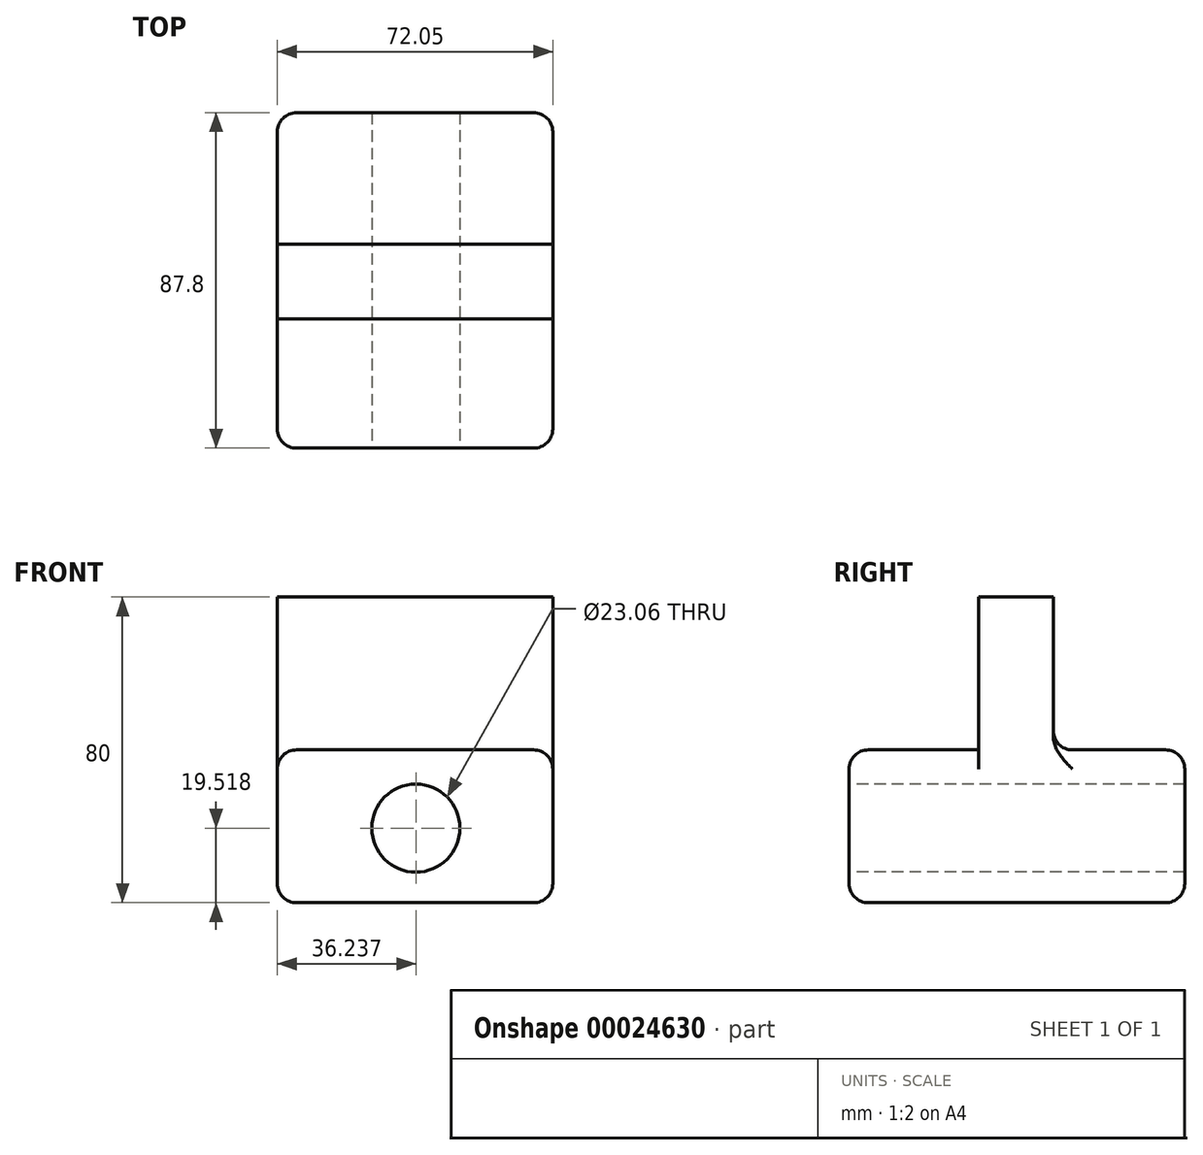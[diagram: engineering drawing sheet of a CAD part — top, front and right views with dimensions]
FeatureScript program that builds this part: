
annotation { "Feature Type Name" : "Feature", "Feature Type Description" : "" }
export const myFeature = defineFeature(function(context is Context, id is Id, definition is map)
    precondition{}
    {
        {
            var Q0;
            Q0=qCreatedBy(makeId("Top.planeOp"),FACE);
            var sketch = newSketch(context, id + "F0", { "sketchPlane" : qUnion([Q0])});
            skLineSegment(sketch, "E0.bottom", {"start": v(-59.89, -44.54) * mm, "end": v(12.16, -44.54) * mm});
            skLineSegment(sketch, "E0.top", {"start": v(-59.89, 43.26) * mm, "end": v(12.16, 43.26) * mm});
            skLineSegment(sketch, "E0.left", {"start": v(-59.89, -44.54) * mm, "end": v(-59.89, 43.26) * mm});
            skLineSegment(sketch, "E0.right", {"start": v(12.16, -44.54) * mm, "end": v(12.16, 43.26) * mm});
            skSolve(sketch);
        }
        {
            var Q0;
            Q0=makeQuery(id+"F0.imprint","IMPRINT",FACE,{"disambiguationData":[TD([[makeQuery(id+"F0.imprint","IMPRINT",EDGE,{"derivedFrom":sQuery(id+"F0.wireOp",EDGE,"E0.bottom")}),1.0]])]});
            extrude(context, id + "F1", {"entities" : qUnion([Q0]), "depth" : 40 * mm});
        }
        {
            var Q0;
            Q0=makeQuery(id+"F1.opExtrude","SWEPT_FACE",FACE,{"disambiguationData":[OSD([sQuery(id+"F0.wireOp",EDGE,"E0.bottom")])]});
            var sketch = newSketch(context, id + "F2", { "sketchPlane" : qUnion([Q0])});
            skCircle(sketch, "E1", {"center": v(-23.65, 19.52) * mm, "radius": 11.53 * mm});
            skSolve(sketch);
        }
        {
            var Q0;
            Q0=makeQuery(id+"F2.imprint","IMPRINT",FACE,{"disambiguationData":[TD([[makeQuery(id+"F2.imprint","IMPRINT",EDGE,{"derivedFrom":sQuery(id+"F2.wireOp",EDGE,"E1")}),1.0]])]});
            extrude(context, id + "F3", {"entities" : qUnion([Q0]), "operationType" : NewBodyOperationType.REMOVE, "endBound" : BoundingType.THROUGH_ALL, "oppositeDirection" : true, "depth" : 25 * mm});
        }
        {
            var Q0;
            Q0=makeQuery(id+"F1.opExtrude","CAP_FACE",FACE,{"disambiguationData":[OSD([sQuery(id+"F0.wireOp",EDGE,"E0.bottom"),sQuery(id+"F0.wireOp",EDGE,"E0.top"),sQuery(id+"F0.wireOp",EDGE,"E0.left"),sQuery(id+"F0.wireOp",EDGE,"E0.right")])],"isStart":false});
            var sketch = newSketch(context, id + "F4", { "sketchPlane" : qUnion([Q0])});
            skLineSegment(sketch, "E2.bottom", {"start": v(-59.89, -10.7) * mm, "end": v(12.16, -10.7) * mm});
            skLineSegment(sketch, "E2.top", {"start": v(-59.89, 8.88) * mm, "end": v(12.16, 8.88) * mm});
            skLineSegment(sketch, "E2.left", {"start": v(-59.89, -10.7) * mm, "end": v(-59.89, 8.88) * mm});
            skLineSegment(sketch, "E2.right", {"start": v(12.16, -10.7) * mm, "end": v(12.16, 8.88) * mm});
            skSolve(sketch);
        }
        {
            var Q0;
            Q0=makeQuery(id+"F4.imprint","IMPRINT",FACE,{"disambiguationData":[TD([[makeQuery(id+"F4.imprint","IMPRINT",EDGE,{"derivedFrom":sQuery(id+"F4.wireOp",EDGE,"E2.bottom")}),1.0]])]});
            extrude(context, id + "F5", {"entities" : qUnion([Q0]), "operationType" : NewBodyOperationType.ADD, "depth" : 40 * mm});
        }
        {
            var Q0;
            Q0=makeQuery(id+"F1.opExtrude","CAP_EDGE",EDGE,{"disambiguationData":[OSD([sQuery(id+"F0.wireOp",EDGE,"E0.bottom")])],"isStart":false});
            var Q1;
            {var subQ0=sQuery(id+"F0.wireOp",EDGE,"E0.right");var subQ1=sQuery(id+"F0.wireOp",EDGE,"E0.bottom");Q1=makeQuery(id+"F5.boolean.opBoolean","SPLIT",EDGE,{"disambiguationData":[TD([makeQuery(id+"F1.opExtrude","SWEPT_FACE",FACE,{"disambiguationData":[OSD([subQ1])]})])],"derivedFrom":makeQuery(id+"F1.opExtrude","CAP_EDGE",EDGE,{"disambiguationData":[OSD([subQ0])],"isStart":false})});}
            var Q2;
            Q2=makeQuery(id+"F1.opExtrude","SWEPT_EDGE",EDGE,{"disambiguationData":[OSD([sQuery(id+"F0.wireOp",EDGE,"E0.bottom"),sQuery(id+"F0.wireOp",EDGE,"E0.right")])]});
            var Q3;
            {var subQ0=sQuery(id+"F0.wireOp",EDGE,"E0.right");var subQ1=sQuery(id+"F0.wireOp",EDGE,"E0.top");Q3=makeQuery(id+"F5.boolean.opBoolean","SPLIT",EDGE,{"disambiguationData":[TD([makeQuery(id+"F1.opExtrude","SWEPT_FACE",FACE,{"disambiguationData":[OSD([subQ1])]})])],"derivedFrom":makeQuery(id+"F1.opExtrude","CAP_EDGE",EDGE,{"disambiguationData":[OSD([subQ0])],"isStart":false})});}
            var Q4;
            Q4=makeQuery(id+"F1.opExtrude","SWEPT_EDGE",EDGE,{"disambiguationData":[OSD([sQuery(id+"F0.wireOp",EDGE,"E0.top"),sQuery(id+"F0.wireOp",EDGE,"E0.right")])]});
            var Q5;
            Q5=makeQuery(id+"F1.opExtrude","CAP_EDGE",EDGE,{"disambiguationData":[OSD([sQuery(id+"F0.wireOp",EDGE,"E0.right")])],"isStart":true});
            var Q6;
            Q6=makeQuery(id+"F1.opExtrude","CAP_EDGE",EDGE,{"disambiguationData":[OSD([sQuery(id+"F0.wireOp",EDGE,"E0.bottom")])],"isStart":true});
            var Q7;
            Q7=makeQuery(id+"F3.boolean.opBoolean","COPY",EDGE,{"derivedFrom":makeQuery(id+"F3.opExtrude","CAP_EDGE",EDGE,{"disambiguationData":[OSD([sQuery(id+"F2.wireOp",EDGE,"E1")])],"isStart":true})});
            var Q8;
            Q8=makeQuery(id+"F1.opExtrude","SWEPT_EDGE",EDGE,{"disambiguationData":[OSD([sQuery(id+"F0.wireOp",EDGE,"E0.bottom"),sQuery(id+"F0.wireOp",EDGE,"E0.left")])]});
            var Q9;
            {var subQ0=sQuery(id+"F0.wireOp",EDGE,"E0.left");var subQ1=sQuery(id+"F0.wireOp",EDGE,"E0.top");Q9=makeQuery(id+"F5.boolean.opBoolean","SPLIT",EDGE,{"disambiguationData":[TD([makeQuery(id+"F1.opExtrude","SWEPT_FACE",FACE,{"disambiguationData":[OSD([subQ1])]})])],"derivedFrom":makeQuery(id+"F1.opExtrude","CAP_EDGE",EDGE,{"disambiguationData":[OSD([subQ0])],"isStart":false})});}
            var Q10;
            {var subQ0=sQuery(id+"F0.wireOp",EDGE,"E0.left");var subQ1=sQuery(id+"F0.wireOp",EDGE,"E0.bottom");Q10=makeQuery(id+"F5.boolean.opBoolean","SPLIT",EDGE,{"disambiguationData":[TD([makeQuery(id+"F1.opExtrude","SWEPT_FACE",FACE,{"disambiguationData":[OSD([subQ1])]})])],"derivedFrom":makeQuery(id+"F1.opExtrude","CAP_EDGE",EDGE,{"disambiguationData":[OSD([subQ0])],"isStart":false})});}
            var Q11;
            Q11=makeQuery(id+"F1.opExtrude","CAP_EDGE",EDGE,{"disambiguationData":[OSD([sQuery(id+"F0.wireOp",EDGE,"E0.left")])],"isStart":true});
            var Q12;
            Q12=makeQuery(id+"F1.opExtrude","SWEPT_EDGE",EDGE,{"disambiguationData":[OSD([sQuery(id+"F0.wireOp",EDGE,"E0.top"),sQuery(id+"F0.wireOp",EDGE,"E0.left")])]});
            var Q13;
            Q13=makeQuery(id+"F1.opExtrude","CAP_EDGE",EDGE,{"disambiguationData":[OSD([sQuery(id+"F0.wireOp",EDGE,"E0.top")])],"isStart":true});
            var Q14;
            Q14=makeQuery(id+"F1.opExtrude","CAP_EDGE",EDGE,{"disambiguationData":[OSD([sQuery(id+"F0.wireOp",EDGE,"E0.top")])],"isStart":false});
            fillet(context, id + "F6", {"entities" : qUnion([Q0, Q1, Q2, Q3, Q4, Q5, Q6, Q7, Q8, Q9, Q10, Q11, Q12, Q13, Q14]), "radius" : 5 * mm, "tangentPropagation" : true, "allowEdgeOverflow" : false});
        }
        {
            var Q0;
            Q0=makeQuery(id+"F5.opExtrude","CAP_EDGE",EDGE,{"disambiguationData":[OSD([sQuery(id+"F4.wireOp",EDGE,"E2.top")])],"isStart":true});
            var Q1;
            Q1=makeQuery(id+"F5.opExtrude","CAP_EDGE",EDGE,{"disambiguationData":[OSD([sQuery(id+"F4.wireOp",EDGE,"E2.bottom")])],"isStart":true});
            fillet(context, id + "F7", {"entities" : qUnion([Q0, Q1]), "radius" : 5 * mm, "tangentPropagation" : true, "allowEdgeOverflow" : false});
        }
    });
